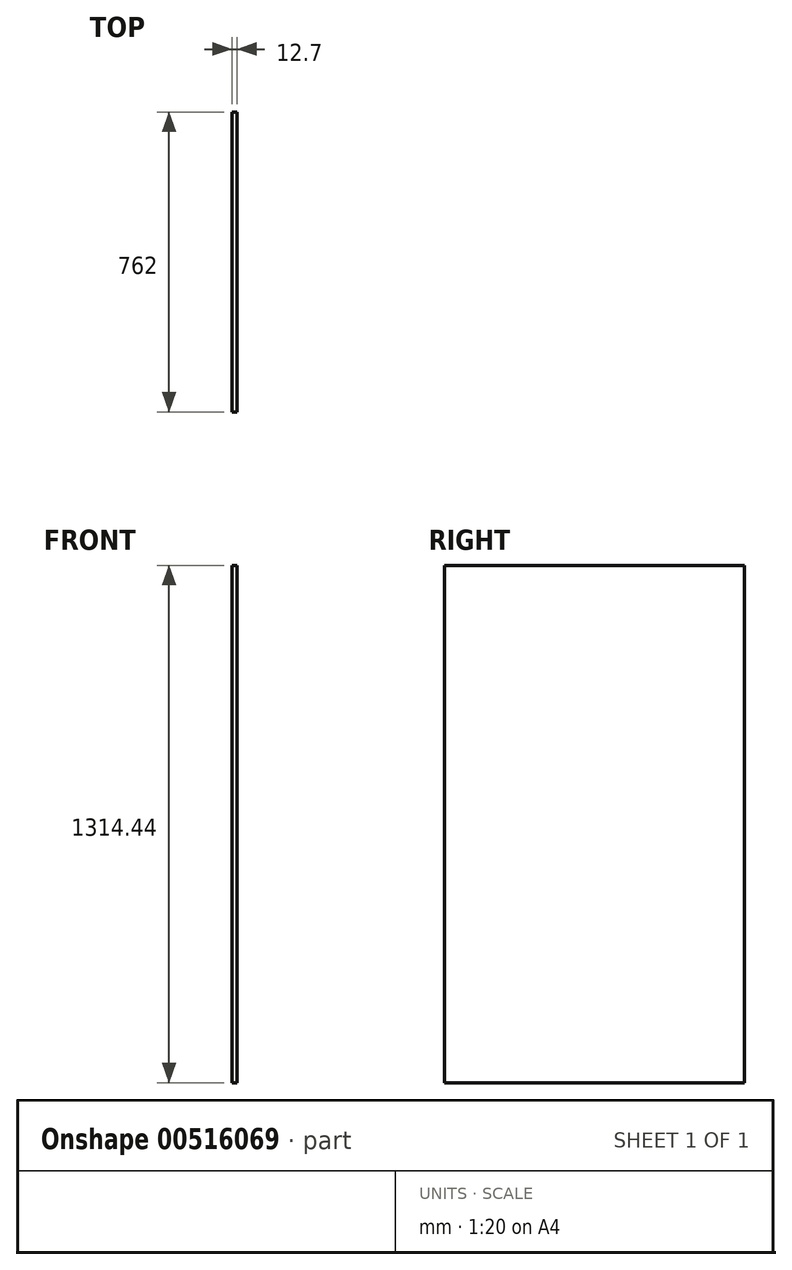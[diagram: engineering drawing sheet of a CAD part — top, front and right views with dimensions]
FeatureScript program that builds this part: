
annotation { "Feature Type Name" : "Feature", "Feature Type Description" : "" }
export const myFeature = defineFeature(function(context is Context, id is Id, definition is map)
    precondition{}
    {
        {
            var Q0;
            Q0=qCreatedBy(makeId("Right.planeOp"),FACE);
            var sketch = newSketch(context, id + "F0", { "sketchPlane" : qUnion([Q0])});
            skLineSegment(sketch, "E0.bottom", {"start": v(381, -657.23) * mm, "end": v(-381, -657.23) * mm});
            skLineSegment(sketch, "E0.top", {"start": v(381, 657.22) * mm, "end": v(-381, 657.22) * mm});
            skLineSegment(sketch, "E0.left", {"start": v(381, -657.23) * mm, "end": v(381, 657.23) * mm});
            skLineSegment(sketch, "E0.right", {"start": v(-381, -657.23) * mm, "end": v(-381, 657.22) * mm});
            skPoint(sketch, "E0.middle", {"position": v(0, 0) * mm});
            skSolve(sketch);
        }
        {
            var Q0;
            Q0=makeQuery(id+"F0.imprint","IMPRINT",FACE,{"disambiguationData":[TD([[makeQuery(id+"F0.imprint","IMPRINT",EDGE,{"derivedFrom":sQuery(id+"F0.wireOp",EDGE,"E0.bottom")}),-1.0]])]});
            extrude(context, id + "F1", {"entities" : qUnion([Q0]), "depth" : 12.7 * mm, "offsetDistance" : 25.4 * mm});
        }
    });
